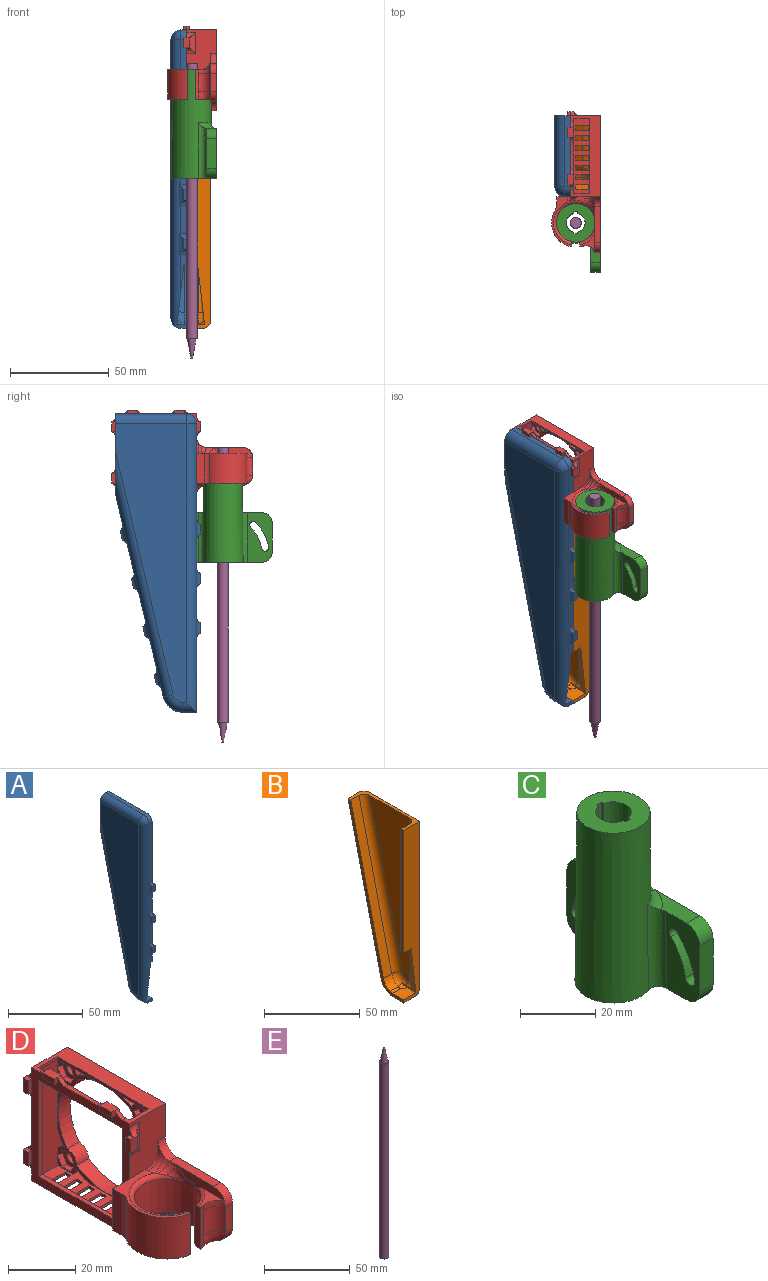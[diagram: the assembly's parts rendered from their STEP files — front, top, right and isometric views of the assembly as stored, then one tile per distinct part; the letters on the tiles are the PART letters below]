
ASSEMBLY  parts=5 mates=1
PART A: 111 faces, bbox 10.2x48.5x152.5 mm
  f0: plane 14.34x3mm, normal (0,-1,0), area 43mm2, adj f20,f34,f100,f101
  f1: plane 14.34x3mm, normal (0,-1,0), area 43mm2, adj f20,f34,f105,f106
  f2: plane 47.98x3mm, normal (0,-1,0), area 143.9mm2, adj f20,f34,f36,f110
  f3: plane 14.91x3.52mm, normal (0,0.97,-0.23), area 45.9mm2, adj f10,f20,f31,f80
  f4: plane 13.96x3.3mm, normal (0,0.97,-0.23), area 43mm2, adj f20,f31,f77,f85
  f5: plane 13.96x3.3mm, normal (0,0.97,-0.23), area 43mm2, adj f20,f31,f82,f90
  f6: plane 4.04x3mm, normal (0,0.97,-0.23), area 12.4mm2, adj f11,f20,f31,f95
  f7: plane 13.96x3.3mm, normal (0,0.97,-0.23), area 43mm2, adj f20,f31,f87,f91
  f8: plane 3x2mm, normal (0,-1,0), area 6mm2, adj f12,f18,f20,f34
  f9: cylinder r=8mm len=5.61mm, axis (1,0,0), area 7.7mm2, adj f14,f20,f26,f39
  f10: plane 41x8mm, normal (0,1,0), area 299.3mm2, adj f3,f19,f20,f22,f23,f31
  f11: cylinder r=10mm len=9.73mm, axis (1,0,0), area 40.2mm2, adj f6,f12,f20,f32
  f12: plane 7.09x3mm, normal (0,0,-1), area 21.3mm2, adj f8,f11,f20,f33
  f13: plane 18.22x3mm, normal (0,-1,0), area 25.7mm2, adj f20,f34,f37,f38,f96
  f14: plane 101.84x24.07mm, normal (0,-0.97,0.23), area 104.6mm2, adj f9,f15,f20,f25
  f15: plane 39x6mm, normal (0,-1,0), area 205.3mm2, adj f14,f16,f20,f21,f24,f25
  f16: plane 31.95x1mm, normal (0,0,-1), area 31.9mm2, adj f15,f20,f24,f30
  f17: plane 112x1mm, normal (0,1,0), area 112mm2, adj f20,f28,f30,f37
  f18: plane 8.12x5mm, normal (0,0,1), area 36.8mm2, adj f8,f20,f34,f38,f39,f40
  f19: plane 36x3mm, normal (0,0,1), area 108mm2, adj f10,f20,f23,f36
  f20: plane 151x43mm, normal (1,0,0), area 665.4mm2, adj f0,f1,f2,f3,f4,f5,f6,f7
  f21: plane 137x31.95mm, normal (1,0,0), area 2536.5mm2, adj f15,f24,f25,f26,f27,f28
  f22: plane 141x36mm, normal (-1,0,0), area 3174.7mm2, adj f10,f23,f31,f32,f33,f34
  f23: cylinder r=5mm len=36mm, axis (0,-1,0), area 282.7mm2, adj f10,f19,f22,f35
  f24: cylinder r=5mm len=31.95mm, axis (0,1,0), area 250.9mm2, adj f15,f16,f21,f29
  f25: cylinder r=5mm len=123.58mm, axis (0,-0.23,-0.97), area 882.3mm2, adj f14,f15,f21,f26
  f26: torus R=3mm, axis (-1,0,0), area 51.6mm2, adj f9,f21,f25,f27,f38,f40
  f27: cylinder r=5mm len=3.34mm, axis (0,-1,0), area 6.3mm2, adj f21,f26,f28,f38
  f28: cylinder r=5mm len=140.25mm, axis (0,0,1), area 1031.4mm2, adj f17,f21,f27,f29,f37,f38
  f29: sphere r=5mm, area 39.3mm2, adj f24,f28,f30
  f30: cylinder r=5mm len=5mm, axis (-1,0,0), area 7.9mm2, adj f16,f17,f20,f29
  f31: cylinder r=5mm len=124.04mm, axis (0,0.23,0.97), area 849.2mm2, adj f3,f4,f5,f6,f7,f10,f22,f32
  f32: torus R=5mm, axis (-1,0,0), area 86mm2, adj f11,f22,f31,f33
  f33: cylinder r=5mm len=7.09mm, axis (0,1,0), area 41.4mm2, adj f12,f22,f32,f34
  f34: cylinder r=5mm len=146mm, axis (0,0,-1), area 1087.2mm2, adj f0,f1,f2,f8,f13,f18,f22,f33
  f35: sphere r=5mm, area 39.3mm2, adj f23,f34,f36
  f36: cylinder r=5mm len=5mm, axis (1,0,0), area 23.6mm2, adj f2,f19,f20,f35
  f37: plane 2.03x1.5mm, normal (0,0,-1), area 3mm2, adj f13,f17,f20,f28,f38
  f38: plane 30.67x10.67mm, normal (0.99,0,-0.12), area 87.8mm2, adj f13,f18,f26,f27,f28,f34,f37,f40
  f39: cylinder r=3.5mm len=1.88mm, axis (1,0,0), area 2mm2, adj f9,f18,f20,f40
  f40: bspline ~4.86x3.6mm, area 11.8mm2, adj f18,f26,f38,f39
  f41: plane 5x1.5mm, normal (0,1,0), area 7.5mm2, adj f20,f42,f44,f45
  f42: plane 2x1.5mm, normal (0,0,1), area 3mm2, adj f20,f41,f43,f45
  f43: plane 5x3mm, normal (0,-1,0), area 15mm2, adj f42,f44,f45,f106,f108,f110
  f44: plane 2x1.5mm, normal (0,0,-1), area 3mm2, adj f20,f41,f43,f45
  f45: plane 5x2mm, normal (1,0,0), area 10mm2, adj f41,f42,f43,f44
  f46: plane 5x1.5mm, normal (0,1,0), area 7.5mm2, adj f20,f47,f49,f50
  f47: plane 2x1.5mm, normal (0,0,1), area 3mm2, adj f20,f46,f48,f50
  f48: plane 5x3mm, normal (0,-1,0), area 15mm2, adj f47,f49,f50,f101,f103,f105
  f49: plane 2x1.5mm, normal (0,0,-1), area 3mm2, adj f20,f46,f48,f50
  f50: plane 5x2mm, normal (1,0,0), area 10mm2, adj f46,f47,f48,f49
  f51: plane 5x1.5mm, normal (0,1,0), area 7.5mm2, adj f20,f52,f54,f55
  f52: plane 2x1.5mm, normal (0,0,1), area 3mm2, adj f20,f51,f53,f55
  f53: plane 5x3mm, normal (0,-1,0), area 15mm2, adj f52,f54,f55,f96,f98,f100
  f54: plane 2x1.5mm, normal (0,0,-1), area 3mm2, adj f20,f51,f53,f55
  f55: plane 5x2mm, normal (1,0,0), area 10mm2, adj f51,f52,f53,f54
  f56: plane 4.87x1.5mm, normal (0,-0.97,0.23), area 7.5mm2, adj f20,f57,f59,f60
  f57: plane 1.95x1.5mm, normal (0,-0.23,-0.97), area 3mm2, adj f20,f56,f58,f60
  f58: plane 4.87x3mm, normal (0,0.97,-0.23), area 15mm2, adj f57,f59,f60,f91,f93,f95
  f59: plane 1.95x1.5mm, normal (0,0.23,0.97), area 3mm2, adj f20,f56,f58,f60
  f60: plane 5.33x3.1mm, normal (1,0,0), area 10mm2, adj f56,f57,f58,f59
  f61: plane 1.95x1.5mm, normal (0,0.23,0.97), area 3mm2, adj f20,f62,f64,f65
  f62: plane 4.87x1.5mm, normal (0,-0.97,0.23), area 7.5mm2, adj f20,f61,f63,f65
  f63: plane 1.95x1.5mm, normal (0,-0.23,-0.97), area 3mm2, adj f20,f62,f64,f65
  f64: plane 4.87x3mm, normal (0,0.97,-0.23), area 15mm2, adj f61,f63,f65,f87,f89,f90
  f65: plane 5.33x3.1mm, normal (1,0,0), area 10mm2, adj f61,f62,f63,f64
  f66: plane 1.95x1.5mm, normal (0,0.23,0.97), area 3mm2, adj f20,f67,f69,f70
  f67: plane 4.87x1.5mm, normal (0,-0.97,0.23), area 7.5mm2, adj f20,f66,f68,f70
  f68: plane 1.95x1.5mm, normal (0,-0.23,-0.97), area 3mm2, adj f20,f67,f69,f70
  f69: plane 4.87x3mm, normal (0,0.97,-0.23), area 15mm2, adj f66,f68,f70,f82,f84,f85
  f70: plane 5.33x3.1mm, normal (1,0,0), area 10mm2, adj f66,f67,f68,f69
  f71: plane 1.95x1.5mm, normal (0,0.23,0.97), area 3mm2, adj f20,f72,f74,f75
  f72: plane 4.87x1.5mm, normal (0,-0.97,0.23), area 7.5mm2, adj f20,f71,f73,f75
  f73: plane 1.95x1.5mm, normal (0,-0.23,-0.97), area 3mm2, adj f20,f72,f74,f75
  f74: plane 4.87x3mm, normal (0,0.97,-0.23), area 15mm2, adj f71,f73,f75,f77,f79,f80
  f75: plane 5.33x3.1mm, normal (1,0,0), area 10mm2, adj f71,f72,f73,f74
  f76: bspline ~2.88x2.77mm, area 0.5mm2, adj f31,f77,f79
  f77: cylinder r=3mm len=3mm, axis (1,0,0), area 9.2mm2, adj f4,f20,f74,f76,f79
  f78: bspline ~3.33x2.88mm, area 0.5mm2, adj f31,f79,f80
  f79: cylinder r=3mm len=10.92mm, axis (0,-0.23,-0.97), area 24.8mm2, adj f31,f74,f76,f77,f78,f80
  f80: cylinder r=3mm len=3.21mm, axis (-1,0,0), area 9.2mm2, adj f3,f20,f74,f78,f79
  f81: bspline ~2.88x2.77mm, area 0.5mm2, adj f31,f82,f84
  f82: cylinder r=3mm len=3mm, axis (1,0,0), area 9.2mm2, adj f5,f20,f69,f81,f84
  f83: bspline ~3.33x2.88mm, area 0.5mm2, adj f31,f84,f85
  f84: cylinder r=3mm len=10.92mm, axis (0,-0.23,-0.97), area 24.8mm2, adj f31,f69,f81,f82,f83,f85
  f85: cylinder r=3mm len=3.21mm, axis (-1,0,0), area 9.2mm2, adj f4,f20,f69,f83,f84
  f86: bspline ~2.88x2.77mm, area 0.5mm2, adj f31,f87,f89
  f87: cylinder r=3mm len=3mm, axis (1,0,0), area 9.2mm2, adj f7,f20,f64,f86,f89
  f88: bspline ~3.33x2.88mm, area 0.5mm2, adj f31,f89,f90
  f89: cylinder r=3mm len=10.92mm, axis (0,-0.23,-0.97), area 24.8mm2, adj f31,f64,f86,f87,f88,f90
  f90: cylinder r=3mm len=3.21mm, axis (-1,0,0), area 9.2mm2, adj f5,f20,f64,f88,f89
  f91: cylinder r=3mm len=3.21mm, axis (-1,0,0), area 9.2mm2, adj f7,f20,f58,f92,f93
  f92: bspline ~3.33x2.88mm, area 0.5mm2, adj f31,f91,f93
  f93: cylinder r=3mm len=10.92mm, axis (0,-0.23,-0.97), area 24.8mm2, adj f31,f58,f91,f92,f94,f95
  f94: bspline ~2.88x2.77mm, area 0.5mm2, adj f31,f93,f95
  f95: cylinder r=3mm len=3mm, axis (1,0,0), area 9.2mm2, adj f6,f20,f58,f93,f94
  f96: cylinder r=3mm len=3mm, axis (1,0,0), area 9.2mm2, adj f13,f20,f53,f97,f98
  f97: bspline ~2.91x2.88mm, area 0.5mm2, adj f34,f96,f98
  f98: cylinder r=3mm len=10.73mm, axis (0,0,1), area 24.8mm2, adj f34,f53,f96,f97,f99,f100
  f99: bspline ~2.91x2.88mm, area 0.5mm2, adj f34,f98,f100
  f100: cylinder r=3mm len=3mm, axis (1,0,0), area 9.2mm2, adj f0,f20,f53,f98,f99
  f101: cylinder r=3mm len=3mm, axis (1,0,0), area 9.2mm2, adj f0,f20,f48,f102,f103
  f102: bspline ~2.91x2.88mm, area 0.5mm2, adj f34,f101,f103
  f103: cylinder r=3mm len=10.73mm, axis (0,0,1), area 24.8mm2, adj f34,f48,f101,f102,f104,f105
  f104: bspline ~2.91x2.88mm, area 0.5mm2, adj f34,f103,f105
  f105: cylinder r=3mm len=3mm, axis (1,0,0), area 9.2mm2, adj f1,f20,f48,f103,f104
  f106: cylinder r=3mm len=3mm, axis (1,0,0), area 9.2mm2, adj f1,f20,f43,f107,f108
  f107: bspline ~2.91x2.88mm, area 0.5mm2, adj f34,f106,f108
  f108: cylinder r=3mm len=10.73mm, axis (0,0,1), area 24.8mm2, adj f34,f43,f106,f107,f109,f110
  f109: bspline ~2.91x2.88mm, area 0.5mm2, adj f34,f108,f110
  f110: cylinder r=3mm len=3mm, axis (1,0,0), area 9.2mm2, adj f2,f20,f43,f108,f109
PART B: 24 faces, bbox 14.1x43.1x113.9 mm
  f0: cylinder r=8mm len=6mm, axis (-1,0,0), area 46.4mm2, adj f2,f3,f17,f23
  f1: plane 110x12mm, normal (0,-1,0), area 1099.1mm2, adj f2,f4,f6,f7,f10,f12,f15,f20
  f2: plane 110x41mm, normal (-1,0,0), area 247.8mm2, adj f0,f1,f3,f4,f6,f7,f8,f9
  f3: plane 101.84x24.07mm, normal (0,-0.97,0.23), area 627.9mm2, adj f0,f2,f6,f16
  f4: plane 9x8.12mm, normal (0,0,1), area 70.5mm2, adj f1,f2,f20,f22,f23
  f5: plane 82.29x6mm, normal (0,1,0), area 469.1mm2, adj f6,f10,f18,f20,f21
  f6: plane 41.4x12.4mm, normal (0,0,1), area 126mm2, adj f1,f2,f3,f5,f9,f10,f11,f12
  f7: plane 8x7.09mm, normal (0,0,-1), area 56.7mm2, adj f1,f2,f8,f15
  f8: cylinder r=10mm len=9.73mm, axis (-1,0,0), area 107.1mm2, adj f2,f7,f9,f14
  f9: plane 102.3x24.18mm, normal (0,0.97,-0.23), area 841mm2, adj f2,f6,f8,f13
  f10: plane 78x2mm, normal (-1,0,0), area 156mm2, adj f1,f5,f6,f21
  f11: plane 104x28.83mm, normal (-1,0,0), area 1718.6mm2, adj f6,f16,f17,f18,f19
  f12: plane 106x36.89mm, normal (1,0,0), area 2578mm2, adj f1,f6,f13,f14,f15
  f13: cylinder r=4mm len=103.22mm, axis (0,-0.23,-0.97), area 657.5mm2, adj f6,f9,f12,f14
  f14: torus R=6mm, axis (1,0,0), area 71.9mm2, adj f8,f12,f13,f15
  f15: cylinder r=4mm len=7.09mm, axis (0,-1,0), area 44.5mm2, adj f1,f7,f12,f14
  f16: cylinder r=4mm len=102.76mm, axis (0,0.23,0.97), area 654.5mm2, adj f3,f6,f11,f17
  f17: torus R=4mm, axis (1,0,0), area 45.4mm2, adj f0,f11,f16,f19,f20,f22
  f18: cylinder r=4mm len=106.8mm, axis (0,0,-1), area 627.6mm2, adj f5,f6,f11,f19,f20
  f19: cylinder r=4mm len=3.89mm, axis (0,1,0), area 7.7mm2, adj f11,f17,f18,f20
  f20: plane 32.13x12.13mm, normal (-0.99,0,-0.12), area 77.9mm2, adj f1,f4,f5,f17,f18,f19,f21,f22
  f21: plane 5.5x2mm, normal (0,0,-1), area 11mm2, adj f1,f5,f10,f20
  f22: bspline ~4.02x3.5mm, area 8.7mm2, adj f4,f17,f20,f23
  f23: cylinder r=3.5mm len=6mm, axis (-1,0,0), area 11.9mm2, adj f0,f2,f4,f22
PART C: 35 faces, bbox 24x50.2x60 mm
  f0: plane 16.51x5.4mm, normal (0,0,1), area 60.5mm2, adj f1,f2,f18,f33,f34
  f1: plane 25x12.78mm, normal (-1,0,0), area 249.6mm2, adj f0,f4,f14,f18,f21,f26,f27,f28
  f2: plane 50.04x25.04mm, normal (1,0,0), area 1116.3mm2, adj f0,f4,f14,f15,f16,f18,f19,f20
  f3: cone r=9.75mm half-angle=0.5deg, axis (0,0,-1), area 2764.5mm2, adj f4,f7,f30,f31,f32,f33,f34
  f4: plane 40.18x22.93mm, normal (0,0,-1), area 425.7mm2, adj f1,f2,f3,f5,f6,f8,f9,f10
  f5: cone r=4.75mm half-angle=0.5deg, axis (0,0,-1), area 764.3mm2, adj f4,f7,f8,f11
  f6: cone r=4.75mm half-angle=0.5deg, axis (0,0,-1), area 764.3mm2, adj f4,f7,f9,f12
  f7: plane 19.5x19.5mm, normal (0,0,1), area 225mm2, adj f3,f5,f6,f8,f9,f10,f11,f12
  f8: plane 55x1.34mm, normal (1,0,0), area 45.7mm2, adj f4,f5,f7,f10
  f9: plane 55x1.34mm, normal (-1,0,0), area 45.7mm2, adj f4,f6,f7,f10
  f10: plane 55x1.8mm, normal (0,1,-0.01), area 99mm2, adj f4,f7,f8,f9
  f11: plane 55x1.34mm, normal (1,0,0), area 45.7mm2, adj f4,f5,f7,f13
  f12: plane 55x1.34mm, normal (-1,0,0), area 45.7mm2, adj f4,f6,f7,f13
  f13: plane 55x1.8mm, normal (0,-1,-0.01), area 99mm2, adj f4,f7,f11,f12
  f14: plane 15x5mm, normal (0,1,0), area 75mm2, adj f1,f2,f18,f21
  f15: plane 16.52x5.41mm, normal (0,0,1), area 60.5mm2, adj f2,f17,f19,f30,f31
  f16: plane 15x5mm, normal (0,-1,0), area 75mm2, adj f2,f17,f19,f20
  f17: plane 25x12.78mm, normal (-1,0,0), area 249.6mm2, adj f4,f15,f16,f19,f20,f22,f23,f24
  f18: cylinder r=5mm len=5mm, axis (1,0,0), area 39.3mm2, adj f0,f1,f2,f14
  f19: cylinder r=5mm len=5mm, axis (-1,0,0), area 39.3mm2, adj f2,f15,f16,f17
  f20: cylinder r=5mm len=5mm, axis (-1,0,0), area 39.3mm2, adj f2,f4,f16,f17
  f21: cylinder r=5mm len=5mm, axis (1,0,0), area 39.3mm2, adj f1,f2,f4,f14
  f22: cylinder r=20mm len=10.67mm, axis (-1,0,0), area 61.1mm2, adj f2,f17,f23,f24
  f23: cylinder r=1.75mm len=5mm, axis (-1,0,0), area 27.5mm2, adj f2,f17,f22,f25
  f24: cylinder r=1.75mm len=5mm, axis (-1,0,0), area 27.5mm2, adj f2,f17,f22,f25
  f25: cylinder r=23.5mm len=12.54mm, axis (-1,0,0), area 71.8mm2, adj f2,f17,f23,f24
  f26: cylinder r=1.75mm len=5mm, axis (-1,0,0), area 27.5mm2, adj f1,f2,f27,f28
  f27: cylinder r=23.5mm len=12.54mm, axis (-1,0,0), area 71.8mm2, adj f1,f2,f26,f29
  f28: cylinder r=20mm len=10.67mm, axis (-1,0,0), area 61.1mm2, adj f1,f2,f26,f29
  f29: cylinder r=1.75mm len=5mm, axis (-1,0,0), area 27.5mm2, adj f1,f2,f27,f28
  f30: bspline ~43.43x4.74mm, area 150.3mm2, adj f3,f4,f15,f17,f31
  f31: torus R=13mm, axis (0,0,-1), area 40.5mm2, adj f3,f15,f30,f32
  f32: bspline ~7.91x3.1mm, area 26.4mm2, adj f2,f3,f31,f33
  f33: torus R=13mm, axis (0,0,-1), area 40.5mm2, adj f0,f3,f32,f34
  f34: bspline ~43.43x4.74mm, area 150.3mm2, adj f0,f1,f3,f4,f33
PART D: 205 faces, bbox 27.4x72.3x44 mm
  f0: plane 41x15mm, normal (0,1,0), area 522.7mm2, adj f1,f11,f56,f78,f192,f193,f194,f195
  f1: plane 41x15mm, normal (0,0,1), area 259mm2, adj f0,f8,f56,f78,f111,f112,f113,f114
  f2: plane 13.34x1.5mm, normal (0,0,1), area 20mm2, adj f78,f111,f201,f203
  f3: plane 0.24x0.17mm, normal (-1,0,0), area 0mm2, adj f9,f55,f162
  f4: plane 19.93x4.98mm, normal (-1,0,0), area 51.5mm2, adj f9,f53,f60,f61,f65,f149,f154
  f5: plane 10.86x2.95mm, normal (-1,0,0), area 10.7mm2, adj f9,f55,f59,f66,f151
  f6: plane 25.34x16.95mm, normal (0,0,1), area 67.7mm2, adj f8,f50,f51,f147,f148,f152,f153,f155
  f7: plane 1x0.1mm, normal (-1,0,0), area 0mm2, adj f62,f64,f158
  f8: plane 20x15mm, normal (0,-1,0), area 224.5mm2, adj f1,f6,f25,f56,f63,f78,f153,f198
  f9: cone r=9.75mm half-angle=0.5deg, axis (0,0,-1), area 713.6mm2, adj f3,f4,f5,f51,f55,f57,f61,f149
  f10: plane 39x10.5mm, normal (0,0,1), area 247.8mm2, adj f13,f14,f15,f28,f35,f36,f37,f39
  f11: plane 41x15mm, normal (0,0,-1), area 501.2mm2, adj f0,f56,f62,f64,f78,f119,f120,f121
  f12: plane 39x10.5mm, normal (0,0,-1), area 57.6mm2, adj f13,f14,f17,f18,f19,f20,f21,f22
  f13: plane 39x10.5mm, normal (0,-1,0), area 361.6mm2, adj f10,f12,f16,f17,f28,f33,f34,f35
  f14: plane 39x10.5mm, normal (0,1,0), area 361.6mm2, adj f10,f12,f21,f23,f24,f26,f27,f28
  f15: cylinder r=20.5mm len=5.27mm, axis (1,0,0), area 11.8mm2, adj f10,f28,f48,f75
  f16: cylinder r=20.5mm len=5.27mm, axis (1,0,0), area 11.8mm2, adj f13,f28,f46,f73
  f17: plane 0.67x0.67mm, normal (-1,0,0), area 0.2mm2, adj f12,f13,f33
  f18: cylinder r=20.5mm len=5.27mm, axis (1,0,0), area 11.8mm2, adj f12,f20,f28,f30
  f19: cylinder r=20.5mm len=5.27mm, axis (1,0,0), area 11.8mm2, adj f12,f22,f28,f32
  f20: plane 6.85x2.59mm, normal (-1,0,0), area 7.5mm2, adj f12,f18,f30
  f21: plane 0.67x0.67mm, normal (-1,0,0), area 0.2mm2, adj f12,f14,f29
  f22: plane 6.85x2.59mm, normal (-1,0,0), area 7.5mm2, adj f12,f19,f32
  f23: plane 6.85x2.59mm, normal (-1,0,0), area 7.5mm2, adj f14,f27,f31
  f24: plane 6.85x2.59mm, normal (-1,0,0), area 7.5mm2, adj f14,f26,f38
  f25: plane 3x1mm, normal (-1,0,0), area 1mm2, adj f8,f63,f153
  f26: cylinder r=20.5mm len=5.27mm, axis (1,0,0), area 11.8mm2, adj f14,f24,f28,f38
  f27: cylinder r=20.5mm len=5.27mm, axis (1,0,0), area 11.8mm2, adj f14,f23,f28,f31
  f28: plane 39x39mm, normal (-1,0,0), area 167.5mm2, adj f10,f12,f13,f14,f15,f16,f18,f19
  f29: cylinder r=4.5mm len=2mm, axis (1,0,0), area 1.9mm2, adj f12,f14,f21,f28
  f30: cylinder r=4.5mm len=2.59mm, axis (1,0,0), area 6.2mm2, adj f12,f18,f20,f28
  f31: cylinder r=4.5mm len=2.59mm, axis (1,0,0), area 6.2mm2, adj f14,f23,f27,f28
  f32: cylinder r=4.5mm len=2.59mm, axis (1,0,0), area 6.2mm2, adj f12,f19,f22,f28
  f33: cylinder r=4.5mm len=2mm, axis (1,0,0), area 1.9mm2, adj f12,f13,f17,f28
  f34: cylinder r=4.5mm len=2.59mm, axis (1,0,0), area 6.2mm2, adj f13,f28,f42,f45
  f35: cylinder r=4.5mm len=2mm, axis (1,0,0), area 1.9mm2, adj f10,f13,f28,f43
  f36: cylinder r=4.5mm len=2.59mm, axis (1,0,0), area 6.2mm2, adj f10,f28,f39,f41
  f37: cylinder r=4.5mm len=2mm, axis (1,0,0), area 1.9mm2, adj f10,f14,f28,f52
  f38: cylinder r=4.5mm len=2.59mm, axis (1,0,0), area 6.2mm2, adj f14,f24,f26,f28
  f39: plane 6.85x2.59mm, normal (-1,0,0), area 7.5mm2, adj f10,f36,f41
  f40: cylinder r=19.35mm len=23.05mm, axis (1,0,0), area 123.4mm2, adj f28,f56,f76,f77
  f41: cylinder r=20.5mm len=5.27mm, axis (1,0,0), area 11.8mm2, adj f10,f28,f36,f39
  f42: plane 6.85x2.59mm, normal (-1,0,0), area 7.5mm2, adj f13,f34,f45
  f43: plane 0.67x0.67mm, normal (-1,0,0), area 0.2mm2, adj f10,f13,f35
  f44: cylinder r=19.35mm len=23.05mm, axis (1,0,0), area 123.4mm2, adj f28,f56,f74,f76
  f45: cylinder r=20.5mm len=5.27mm, axis (1,0,0), area 11.8mm2, adj f13,f28,f34,f42
  f46: plane 6.85x2.59mm, normal (-1,0,0), area 7.5mm2, adj f13,f16,f73
  f47: cylinder r=19.35mm len=23.05mm, axis (1,0,0), area 123.4mm2, adj f28,f56,f72,f74
  f48: plane 6.85x2.59mm, normal (-1,0,0), area 7.5mm2, adj f10,f15,f75
  f49: plane 25.34x17.78mm, normal (0,0,-1), area 64.2mm2, adj f50,f51,f62,f147,f148,f150,f158,f159
  f50: cylinder r=12.25mm len=18.72mm, axis (0,0,-1), area 363.7mm2, adj f6,f49,f51,f163
  f51: plane 15.1x2.63mm, normal (1,0,0), area 36.1mm2, adj f6,f9,f49,f50,f150,f152
  f52: plane 0.67x0.67mm, normal (-1,0,0), area 0.2mm2, adj f10,f14,f37
  f53: plane 18.51x3.17mm, normal (0,0,1), area 55mm2, adj f4,f56,f63,f65,f156
  f54: plane 9x3mm, normal (0,-1,0), area 27mm2, adj f56,f65,f66,f165
  f55: plane 19.15x3.82mm, normal (0,0,-1), area 53.5mm2, adj f3,f5,f9,f56,f64,f66,f161
  f56: plane 69.34x41mm, normal (1,0,0), area 1023.5mm2, adj f0,f1,f8,f11,f40,f44,f47,f53
  f57: plane 15.1x2.63mm, normal (-1,0,0), area 36.1mm2, adj f9,f58,f59,f60,f149,f151
  f58: cylinder r=12.25mm len=15mm, axis (0,0,-1), area 21.7mm2, adj f57,f59,f60,f164,f165,f166
  f59: plane 8.49x7.82mm, normal (0,0,-1), area 17.9mm2, adj f5,f57,f58,f151,f164
  f60: plane 8.86x7.74mm, normal (0,0,1), area 21.3mm2, adj f4,f57,f58,f149,f166
  f61: plane 4.4x0.25mm, normal (0,0,-1), area 0.7mm2, adj f4,f9,f154
  f62: plane 12x6mm, normal (0,-1,0), area 66.6mm2, adj f7,f11,f49,f78,f158
  f63: cylinder r=5mm len=5mm, axis (-1,0,0), area 23.6mm2, adj f8,f25,f53,f56,f155,f157
  f64: cylinder r=5mm len=5mm, axis (1,0,0), area 23.6mm2, adj f7,f11,f55,f56,f159,f160
  f65: cylinder r=5mm len=5mm, axis (1,0,0), area 23.6mm2, adj f4,f53,f54,f56,f166
  f66: cylinder r=5mm len=5mm, axis (-1,0,0), area 23.6mm2, adj f5,f54,f55,f56,f164
  f67: cylinder r=19.35mm len=23.05mm, axis (1,0,0), area 123.4mm2, adj f28,f56,f72,f77
  f68: cylinder r=1.75mm len=3.5mm, axis (1,0,0), area 33mm2, adj f56,f103
  f69: cylinder r=1.75mm len=3.5mm, axis (1,0,0), area 33mm2, adj f56,f95
  f70: cylinder r=1.75mm len=3.5mm, axis (1,0,0), area 33mm2, adj f56,f87
  f71: cylinder r=1.75mm len=3.5mm, axis (1,0,0), area 33mm2, adj f56,f79
  f72: cylinder r=4.5mm len=5mm, axis (1,0,0), area 30.8mm2, adj f28,f47,f56,f67
  f73: cylinder r=4.5mm len=2.59mm, axis (1,0,0), area 6.2mm2, adj f13,f16,f28,f46
  f74: cylinder r=4.5mm len=5mm, axis (1,0,0), area 30.8mm2, adj f28,f44,f47,f56
  f75: cylinder r=4.5mm len=2.59mm, axis (1,0,0), area 6.2mm2, adj f10,f15,f28,f48
  f76: cylinder r=4.5mm len=5mm, axis (1,0,0), area 30.8mm2, adj f28,f40,f44,f56
  f77: cylinder r=4.5mm len=5mm, axis (1,0,0), area 30.8mm2, adj f28,f40,f56,f67
  f78: plane 45x43mm, normal (-1,0,0), area 471.3mm2, adj f0,f1,f2,f8,f11,f62,f115,f116
  f79: plane 7.22x6.25mm, normal (-1,0,0), area 24.2mm2, adj f71,f81,f82,f83,f84,f85,f86
  f80: plane 0.38x0.11mm, normal (1,0,0), area 0mm2, adj f14,f81,f82
  f81: plane 3.13x2mm, normal (0,0.87,0.5), area 7.2mm2, adj f28,f79,f80,f82,f84
  f82: plane 3.13x2mm, normal (0,0.87,-0.5), area 7.2mm2, adj f28,f79,f80,f81,f83
  f83: plane 3.61x2mm, normal (0,0,-1), area 7.2mm2, adj f28,f79,f82,f85
  f84: plane 3.61x2mm, normal (0,0,1), area 7.2mm2, adj f28,f79,f81,f86
  f85: plane 3.13x2mm, normal (0,-0.87,-0.5), area 7.2mm2, adj f28,f79,f83,f86
  f86: plane 3.13x2mm, normal (0,-0.87,0.5), area 7.2mm2, adj f28,f79,f84,f85
  f87: plane 7.22x6.25mm, normal (-1,0,0), area 24.2mm2, adj f70,f89,f90,f91,f92,f93,f94
  f88: plane 0.38x0.11mm, normal (1,0,0), area 0mm2, adj f13,f89,f90
  f89: plane 3.13x2mm, normal (0,-0.87,-0.5), area 7.2mm2, adj f28,f87,f88,f90,f92
  f90: plane 3.13x2mm, normal (0,-0.87,0.5), area 7.2mm2, adj f28,f87,f88,f89,f91
  f91: plane 3.61x2mm, normal (0,0,1), area 7.2mm2, adj f28,f87,f90,f93
  f92: plane 3.61x2mm, normal (0,0,-1), area 7.2mm2, adj f28,f87,f89,f94
  f93: plane 3.13x2mm, normal (0,0.87,0.5), area 7.2mm2, adj f28,f87,f91,f94
  f94: plane 3.13x2mm, normal (0,0.87,-0.5), area 7.2mm2, adj f28,f87,f92,f93
  f95: plane 7.22x6.25mm, normal (-1,0,0), area 24.2mm2, adj f69,f97,f98,f99,f100,f101,f102
  f96: plane 0.38x0.11mm, normal (1,0,0), area 0mm2, adj f13,f97,f98
  f97: plane 3.13x2mm, normal (0,-0.87,-0.5), area 7.2mm2, adj f28,f95,f96,f98,f100
  f98: plane 3.13x2mm, normal (0,-0.87,0.5), area 7.2mm2, adj f28,f95,f96,f97,f99
  f99: plane 3.61x2mm, normal (0,0,1), area 7.2mm2, adj f28,f95,f98,f101
  f100: plane 3.61x2mm, normal (0,0,-1), area 7.2mm2, adj f28,f95,f97,f102
  f101: plane 3.13x2mm, normal (0,0.87,0.5), area 7.2mm2, adj f28,f95,f99,f102
  f102: plane 3.13x2mm, normal (0,0.87,-0.5), area 7.2mm2, adj f28,f95,f100,f101
  f103: plane 7.22x6.25mm, normal (-1,0,0), area 24.2mm2, adj f68,f105,f106,f107,f108,f109,f110
  f104: plane 0.38x0.11mm, normal (1,0,0), area 0mm2, adj f14,f108,f110
  f105: plane 3.61x2mm, normal (0,0,-1), area 7.2mm2, adj f28,f103,f106,f108
  f106: plane 3.13x2mm, normal (0,-0.87,-0.5), area 7.2mm2, adj f28,f103,f105,f107
  f107: plane 3.13x2mm, normal (0,-0.87,0.5), area 7.2mm2, adj f28,f103,f106,f109
  f108: plane 3.13x2mm, normal (0,0.87,-0.5), area 7.2mm2, adj f28,f103,f104,f105,f110
  f109: plane 3.61x2mm, normal (0,0,1), area 7.2mm2, adj f28,f103,f107,f110
  f110: plane 3.13x2mm, normal (0,0.87,0.5), area 7.2mm2, adj f28,f103,f104,f108,f109
  f111: plane 42x39mm, normal (1,0,0), area 360.1mm2, adj f1,f2,f10,f12,f13,f14,f112,f113
  f112: plane 8x1mm, normal (0,-1,0), area 8mm2, adj f1,f12,f111,f114
  f113: plane 8x1mm, normal (0,1,0), area 8mm2, adj f1,f12,f111,f114
  f114: plane 38x1mm, normal (-1,0,0), area 38mm2, adj f1,f12,f112,f113
  f115: plane 35x1.5mm, normal (0,1,0), area 52.5mm2, adj f78,f111,f116,f117
  f116: plane 35x1.5mm, normal (0,0,-1), area 52.5mm2, adj f78,f111,f115,f118
  f117: plane 35x1.5mm, normal (0,0,1), area 52.5mm2, adj f78,f111,f115,f118
  f118: plane 35x1.5mm, normal (0,-1,0), area 52.5mm2, adj f78,f111,f116,f117
  f119: plane 2.5x1mm, normal (1,0,0), area 2.5mm2, adj f10,f11,f120,f122
  f120: plane 6.5x1mm, normal (0,1,0), area 6.5mm2, adj f10,f11,f119,f121
  f121: plane 2.5x1mm, normal (-1,0,0), area 2.5mm2, adj f10,f11,f120,f122
  f122: plane 6.5x1mm, normal (0,-1,0), area 6.5mm2, adj f10,f11,f119,f121
  f123: plane 2.5x1mm, normal (1,0,0), area 2.5mm2, adj f10,f11,f124,f126
  f124: plane 6.5x1mm, normal (0,1,0), area 6.5mm2, adj f10,f11,f123,f125
  f125: plane 2.5x1mm, normal (-1,0,0), area 2.5mm2, adj f10,f11,f124,f126
  f126: plane 6.5x1mm, normal (0,-1,0), area 6.5mm2, adj f10,f11,f123,f125
  f127: plane 2.5x1mm, normal (1,0,0), area 2.5mm2, adj f10,f11,f128,f130
  f128: plane 6.5x1mm, normal (0,1,0), area 6.5mm2, adj f10,f11,f127,f129
  f129: plane 2.5x1mm, normal (-1,0,0), area 2.5mm2, adj f10,f11,f128,f130
  f130: plane 6.5x1mm, normal (0,-1,0), area 6.5mm2, adj f10,f11,f127,f129
  f131: plane 2.5x1mm, normal (1,0,0), area 2.5mm2, adj f10,f11,f132,f134
  f132: plane 6.5x1mm, normal (0,1,0), area 6.5mm2, adj f10,f11,f131,f133
  f133: plane 2.5x1mm, normal (-1,0,0), area 2.5mm2, adj f10,f11,f132,f134
  f134: plane 6.5x1mm, normal (0,-1,0), area 6.5mm2, adj f10,f11,f131,f133
  f135: plane 2.5x1mm, normal (1,0,0), area 2.5mm2, adj f10,f11,f136,f138
  f136: plane 6.5x1mm, normal (0,1,0), area 6.5mm2, adj f10,f11,f135,f137
  f137: plane 2.5x1mm, normal (-1,0,0), area 2.5mm2, adj f10,f11,f136,f138
  f138: plane 6.5x1mm, normal (0,-1,0), area 6.5mm2, adj f10,f11,f135,f137
  f139: plane 2.5x1mm, normal (1,0,0), area 2.5mm2, adj f10,f11,f140,f142
  f140: plane 6.5x1mm, normal (0,1,0), area 6.5mm2, adj f10,f11,f139,f141
  f141: plane 2.5x1mm, normal (-1,0,0), area 2.5mm2, adj f10,f11,f140,f142
  f142: plane 6.5x1mm, normal (0,-1,0), area 6.5mm2, adj f10,f11,f139,f141
  f143: plane 6.5x1mm, normal (0,-1,0), area 6.5mm2, adj f10,f11,f144,f146
  f144: plane 2.5x1mm, normal (1,0,0), area 2.5mm2, adj f10,f11,f143,f145
  f145: plane 6.5x1mm, normal (0,1,0), area 6.5mm2, adj f10,f11,f144,f146
  f146: plane 2.5x1mm, normal (-1,0,0), area 2.5mm2, adj f10,f11,f143,f145
  f147: plane 15x7mm, normal (0,1,0), area 105mm2, adj f6,f49,f78,f148
  f148: plane 15x3.91mm, normal (-1,0,0), area 58.6mm2, adj f6,f49,f147,f163
  f149: torus R=11.26mm, axis (0,0,1), area 23.8mm2, adj f4,f9,f57,f60
  f150: torus R=11.37mm, axis (0,0,1), area 93.1mm2, adj f9,f49,f51,f160,f161,f162
  f151: torus R=11.37mm, axis (0,0,1), area 23.1mm2, adj f5,f9,f57,f59
  f152: torus R=11.26mm, axis (0,0,1), area 91mm2, adj f6,f9,f51,f154,f156,f157
  f153: cylinder r=5mm len=5mm, axis (0,1,0), area 7.9mm2, adj f6,f8,f25,f155
  f154: bspline ~6.38x5.36mm, area 14.2mm2, adj f4,f9,f61,f152,f156
  f155: bspline ~5x5mm, area 11.1mm2, adj f6,f63,f153,f157
  f156: bspline ~5.36x4.4mm, area 12.1mm2, adj f53,f152,f154,f157
  f157: bspline ~5.11x4.51mm, area 10.6mm2, adj f63,f152,f155,f156
  f158: cylinder r=5mm len=5mm, axis (0,-1,0), area 0.8mm2, adj f7,f49,f62,f159
  f159: bspline ~5.19x5.18mm, area 11.9mm2, adj f49,f64,f158,f160
  f160: bspline ~5.05x4.18mm, area 11.4mm2, adj f64,f150,f159,f161
  f161: bspline ~6.64x3.04mm, area 10.4mm2, adj f55,f150,f160,f162
  f162: bspline ~4.33x3.62mm, area 3.3mm2, adj f3,f9,f150,f161
  f163: cylinder r=5mm len=15mm, axis (0,0,-1), area 42.9mm2, adj f6,f49,f50,f148
  f164: bspline ~8.89x6.14mm, area 30.9mm2, adj f58,f59,f66,f165
  f165: cylinder r=5mm len=9mm, axis (0,0,1), area 69.5mm2, adj f54,f58,f164,f166
  f166: bspline ~6.14x3.55mm, area 15mm2, adj f58,f60,f65,f165
  f167: plane 5x1.5mm, normal (0,0,-1), area 7.5mm2, adj f78,f168,f170,f171
  f168: plane 2x1.5mm, normal (0,1,0), area 3mm2, adj f78,f167,f169,f171
  f169: plane 5x3mm, normal (0,0,1), area 15mm2, adj f111,f168,f170,f171,f203,f204
  f170: plane 2x1.5mm, normal (0,-1,0), area 3mm2, adj f78,f167,f169,f171
  f171: plane 5x2mm, normal (-1,0,0), area 10mm2, adj f167,f168,f169,f170
  f172: plane 5x1.5mm, normal (0,0,-1), area 7.5mm2, adj f78,f173,f175,f176
  f173: plane 2x1.5mm, normal (0,1,0), area 3mm2, adj f78,f172,f174,f176
  f174: plane 5x3mm, normal (0,0,1), area 15mm2, adj f111,f173,f175,f176,f201,f202
  f175: plane 2x1.5mm, normal (0,-1,0), area 3mm2, adj f78,f172,f174,f176
  f176: plane 5x2mm, normal (-1,0,0), area 10mm2, adj f172,f173,f174,f175
  f177: plane 5x1.5mm, normal (0,1,0), area 7.5mm2, adj f78,f178,f180,f181
  f178: plane 2x1.5mm, normal (0,0,1), area 3mm2, adj f78,f177,f179,f181
  f179: plane 5x3mm, normal (0,-1,0), area 15mm2, adj f178,f180,f181,f198,f199,f200
  f180: plane 2x1.5mm, normal (0,0,-1), area 3mm2, adj f78,f177,f179,f181
  f181: plane 5x2mm, normal (-1,0,0), area 10mm2, adj f177,f178,f179,f180
  f182: plane 5x1.5mm, normal (0,-1,0), area 7.5mm2, adj f78,f183,f184,f186
  f183: plane 2x1.5mm, normal (0,0,1), area 3mm2, adj f78,f182,f185,f186
  f184: plane 2x1.5mm, normal (0,0,-1), area 3mm2, adj f78,f182,f185,f186
  f185: plane 5x3mm, normal (0,1,0), area 15mm2, adj f183,f184,f186,f195,f196,f197
  f186: plane 5x2mm, normal (-1,0,0), area 10mm2, adj f182,f183,f184,f185
  f187: plane 5x1.5mm, normal (0,-1,0), area 7.5mm2, adj f78,f188,f189,f191
  f188: plane 2x1.5mm, normal (0,0,1), area 3mm2, adj f78,f187,f190,f191
  f189: plane 2x1.5mm, normal (0,0,-1), area 3mm2, adj f78,f187,f190,f191
  f190: plane 5x3mm, normal (0,1,0), area 15mm2, adj f188,f189,f191,f192,f193,f194
  f191: plane 5x2mm, normal (-1,0,0), area 10mm2, adj f187,f188,f189,f190
  f192: cylinder r=3mm len=4.33mm, axis (-1,0,0), area 10.8mm2, adj f0,f78,f190,f193
  f193: cylinder r=3mm len=10.66mm, axis (0,0,-1), area 28.9mm2, adj f0,f190,f192,f194
  f194: cylinder r=3mm len=4.33mm, axis (-1,0,0), area 10.8mm2, adj f0,f78,f190,f193
  f195: cylinder r=3mm len=4.33mm, axis (-1,0,0), area 10.8mm2, adj f0,f78,f185,f196
  f196: cylinder r=3mm len=10.66mm, axis (0,0,-1), area 28.9mm2, adj f0,f185,f195,f197
  f197: cylinder r=3mm len=4.33mm, axis (-1,0,0), area 10.8mm2, adj f0,f78,f185,f196
  f198: cylinder r=3mm len=4.33mm, axis (1,0,0), area 10.8mm2, adj f8,f78,f179,f199
  f199: cylinder r=3mm len=10.66mm, axis (0,0,-1), area 28.9mm2, adj f8,f179,f198,f200
  f200: cylinder r=3mm len=4.33mm, axis (1,0,0), area 10.8mm2, adj f8,f78,f179,f199
  f201: cylinder r=3mm len=2.83mm, axis (1,0,0), area 5.5mm2, adj f2,f78,f111,f174
  f202: cylinder r=3mm len=2.83mm, axis (1,0,0), area 5.5mm2, adj f1,f78,f111,f174
  f203: cylinder r=3mm len=2.83mm, axis (1,0,0), area 5.5mm2, adj f2,f78,f111,f169
  f204: cylinder r=3mm len=2.83mm, axis (1,0,0), area 5.5mm2, adj f1,f78,f111,f169
PART E: 5 faces, bbox 5.5x5.5x149 mm
  f0: cylinder r=2.75mm len=139mm, axis (0,0,-1), area 2401.7mm2, adj f1,f2
  f1: plane 5.5x5.5mm, normal (0,0,1), area 7.7mm2, adj f0,f4
  f2: plane 5.5x5.5mm, normal (0,0,-1), area 23.8mm2, adj f0
  f3: plane 1x1mm, normal (0,0,1), area 0.8mm2, adj f4
  f4: cone r=0.5mm half-angle=10deg, axis (0,0,-1), area 88.1mm2, adj f1,f3
PLACE A at identity
PLACE B at identity
PLACE C at identity fixed
PLACE D at identity fixed
PLACE E rot(axis=(0,1,0),180deg) t=(0,0,58)mm
MATE slider E.f0 <-> C.f5  axis (0,0,1) through (0,0,58)mm
